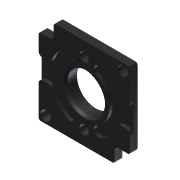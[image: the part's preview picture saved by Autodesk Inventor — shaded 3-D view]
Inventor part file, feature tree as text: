
AUTODESK INVENTOR PART (.ipt)
format: ipt  version: 2013 (Build 170138000, 138)  size: 261,120 bytes
history: native  units: in
note: dims shown in document units (in); Inventor stores cm internally (conversion verified against a paired STEP export)
features: fillet x1, other x1, imported_body x1
ambient origin geometry x8: Origin, YZ Plane, XZ Plane, XY Plane, X Axis, Y Axis, Z Axis, Center Point
feature tree (3):
  fillet  "Fillet4"  [1 undecoded]
  other  "217-2822-775 Mounting Plate STEP1"
  imported_body  "Base1"
note: 1 required parameter value undecoded (feature->parameter linkage not recoverable at this tier; creation-order binding heuristic only, values carry confidence <= 0.55)
